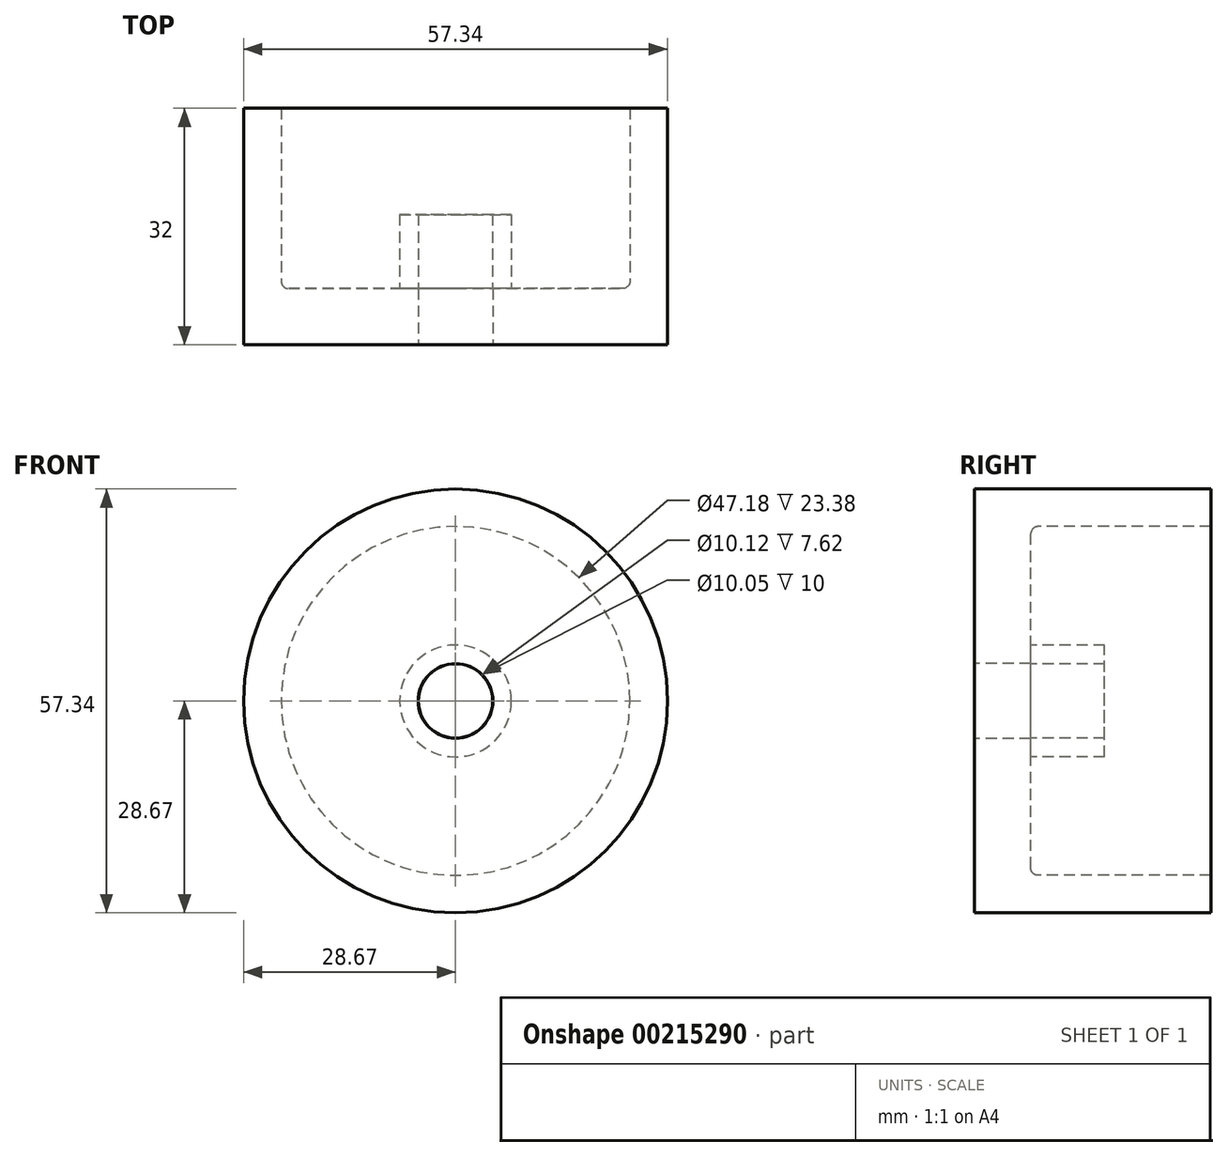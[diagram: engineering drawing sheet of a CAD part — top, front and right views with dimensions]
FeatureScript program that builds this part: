
annotation { "Feature Type Name" : "Feature", "Feature Type Description" : "" }
export const myFeature = defineFeature(function(context is Context, id is Id, definition is map)
    precondition{}
    {
        {
            var Q0;
            Q0=qCreatedBy(makeId("Right.planeOp"),FACE);
            var sketch = newSketch(context, id + "F0", { "sketchPlane" : qUnion([Q0])});
            skLineSegment(sketch, "E0", {"start": v(0, 5.06) * mm, "end": v(0, 28.67) * mm});
            skLineSegment(sketch, "E1", {"start": v(0, 28.67) * mm, "end": v(32, 28.67) * mm});
            skLineSegment(sketch, "E2", {"start": v(32, 28.67) * mm, "end": v(32, 23.6) * mm});
            skLineSegment(sketch, "E3", {"start": v(32, 23.6) * mm, "end": v(8.62, 23.6) * mm});
            skLineSegment(sketch, "E4", {"start": v(7.62, 22.6) * mm, "end": v(7.62, 7.56) * mm});
            skLineSegment(sketch, "E5", {"start": v(7.62, 7.56) * mm, "end": v(17.62, 7.56) * mm});
            skLineSegment(sketch, "E6", {"start": v(17.62, 7.56) * mm, "end": v(17.62, 5.02) * mm});
            skLineSegment(sketch, "E7", {"start": v(17.62, 5.02) * mm, "end": v(7.62, 5.02) * mm});
            skLineSegment(sketch, "E8", {"start": v(7.62, 5.06) * mm, "end": v(7.62, 5.02) * mm});
            skLineSegment(sketch, "E9", {"start": v(7.62, 5.06) * mm, "end": v(0, 5.06) * mm});
            skPoint(sketch, "E10.visualSharp", {"position": v(7.62, 23.6) * mm});
            skArc(sketch, "E10.filletArc", {"start": v(8.62, 23.6) * mm, "mid": v(7.91, 23.3) * mm, "end": v(7.62, 22.6) * mm});
            skLineSegment(sketch, "E11", {"start": v(-75.56, 0) * mm, "end": v(74.23, 0) * mm, "construction": true});
            skSolve(sketch);
        }
        {
            var Q0;
            Q0 = qSketchRegion(id + "F0", true);
            var Q1;
            Q1=sQuery(id+"F0.wireOp",EDGE,"E11");
            revolve(context, id + "F1", {"entities" : qUnion([Q0]), "axis" : qUnion([Q1]), "revolveType" : RevolveType.FULL});
        }
    });
